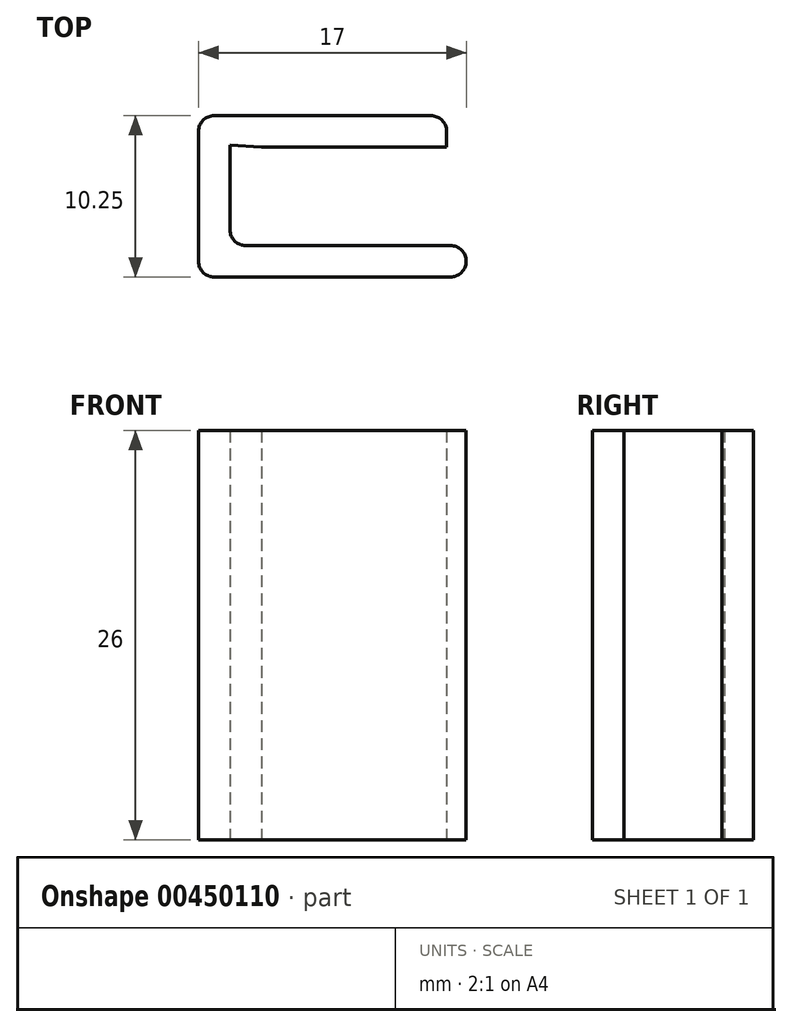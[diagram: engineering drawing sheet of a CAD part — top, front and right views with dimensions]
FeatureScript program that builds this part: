
annotation { "Feature Type Name" : "Feature", "Feature Type Description" : "" }
export const myFeature = defineFeature(function(context is Context, id is Id, definition is map)
    precondition{}
    {
        {
            var Q0;
            Q0=qCreatedBy(makeId("Top.planeOp"),FACE);
            var sketch = newSketch(context, id + "F0", { "sketchPlane" : qUnion([Q0])});
            skLineSegment(sketch, "E0", {"start": v(-15.32, 0) * mm, "end": v(-0.32, 0) * mm});
            skLineSegment(sketch, "E1", {"start": v(0.68, 1) * mm, "end": v(0.68, 1) * mm});
            skLineSegment(sketch, "E2", {"start": v(-0.32, 2) * mm, "end": v(-13.32, 2) * mm});
            skLineSegment(sketch, "E3", {"start": v(-16.32, 1) * mm, "end": v(-16.32, 9.25) * mm});
            skLineSegment(sketch, "E4", {"start": v(-14.32, 3) * mm, "end": v(-14.32, 8.4) * mm});
            skLineSegment(sketch, "E5", {"start": v(-15.32, 10.25) * mm, "end": v(-1.56, 10.25) * mm});
            skLineSegment(sketch, "E6", {"start": v(-0.56, 9.25) * mm, "end": v(-0.56, 8.95) * mm});
            skPoint(sketch, "E7.visualSharp", {"position": v(-0.56, 6.76) * mm});
            skPoint(sketch, "E8.visualSharp", {"position": v(-0.56, 10.25) * mm});
            skArc(sketch, "E8.filletArc", {"start": v(-0.56, 9.25) * mm, "mid": v(-0.86, 9.96) * mm, "end": v(-1.56, 10.25) * mm});
            skPoint(sketch, "E9.visualSharp", {"position": v(-22.56, 10.25) * mm});
            skArc(sketch, "E9.filletArc", {"start": v(-15.32, 10.25) * mm, "mid": v(-16.03, 9.96) * mm, "end": v(-16.32, 9.25) * mm});
            skPoint(sketch, "E10.visualSharp", {"position": v(-14.32, 10) * mm});
            skArc(sketch, "E10.filletArc", {"start": v(-12.33, 8.25) * mm, "mid": v(-13.25, 9.4) * mm, "end": v(-14.32, 8.4) * mm});
            skPoint(sketch, "E11.visualSharp", {"position": v(0.68, 2) * mm});
            skArc(sketch, "E11.filletArc", {"start": v(0.68, 1) * mm, "mid": v(0.38, 1.7) * mm, "end": v(-0.32, 2) * mm});
            skPoint(sketch, "E12.visualSharp", {"position": v(0.68, 0) * mm});
            skArc(sketch, "E12.filletArc", {"start": v(-0.32, 0) * mm, "mid": v(0.38, 0.3) * mm, "end": v(0.68, 1) * mm});
            skPoint(sketch, "E13.visualSharp", {"position": v(-16.32, 0) * mm});
            skArc(sketch, "E13.filletArc", {"start": v(-16.32, 1) * mm, "mid": v(-16.03, 0.3) * mm, "end": v(-15.32, 0) * mm});
            skPoint(sketch, "E14.visualSharp", {"position": v(-14.32, 2) * mm});
            skArc(sketch, "E14.filletArc", {"start": v(-14.32, 3) * mm, "mid": v(-14.03, 2.3) * mm, "end": v(-13.32, 2) * mm});
            skPoint(sketch, "E15.orphan", {"position": v(-4.18, 8.81) * mm});
            skLineSegment(sketch, "E16", {"start": v(-0.56, 8.95) * mm, "end": v(-0.56, 9.25) * mm});
            skLineSegment(sketch, "E17.bottom", {"start": v(-44.93, 10.96) * mm, "end": v(-37.9, 10.96) * mm});
            skLineSegment(sketch, "E17.top", {"start": v(-44.93, 2.89) * mm, "end": v(-36.9, 2.89) * mm});
            skLineSegment(sketch, "E17.left", {"start": v(-44.93, 10.96) * mm, "end": v(-44.93, 2.89) * mm});
            skLineSegment(sketch, "E17.right", {"start": v(-36.9, 9.96) * mm, "end": v(-36.9, 2.89) * mm});
            skPoint(sketch, "E18.visualSharp", {"position": v(-36.9, 10.96) * mm});
            skArc(sketch, "E18.filletArc", {"start": v(-36.9, 9.96) * mm, "mid": v(-37.19, 10.67) * mm, "end": v(-37.9, 10.96) * mm});
            skPoint(sketch, "E19.end.orphan", {"position": v(-0.14, 8.25) * mm});
            skPoint(sketch, "E20.end.orphan", {"position": v(-0.56, 8.25) * mm});
            skLineSegment(sketch, "E21", {"start": v(-12.33, 8.25) * mm, "end": v(-0.56, 8.25) * mm});
            skLineSegment(sketch, "E22", {"start": v(-0.56, 8.95) * mm, "end": v(-0.56, 8.25) * mm});
            skLineSegment(sketch, "E23", {"start": v(-14.32, 8.4) * mm, "end": v(-12.33, 8.25) * mm});
            skSolve(sketch);
        }
        {
            var Q0;
            Q0=makeQuery(id+"F0.imprint","IMPRINT",FACE,{"disambiguationData":[TD([[makeQuery(id+"F0.imprint","IMPRINT",EDGE,{"derivedFrom":sQuery(id+"F0.wireOp",EDGE,"E0")}),1.0]])]});
            var Q1;
            Q1=makeQuery(id+"F0.imprint","IMPRINT",FACE,{"disambiguationData":[TD([[makeQuery(id+"F0.imprint","IMPRINT",EDGE,{"derivedFrom":sQuery(id+"F0.wireOp",EDGE,"E10.filletArc")}),1.0]])]});
            extrude(context, id + "F1", {"entities" : qUnion([Q0, Q1]), "offsetDistance" : 25 * mm, "depth" : 26 * mm});
        }
    });
